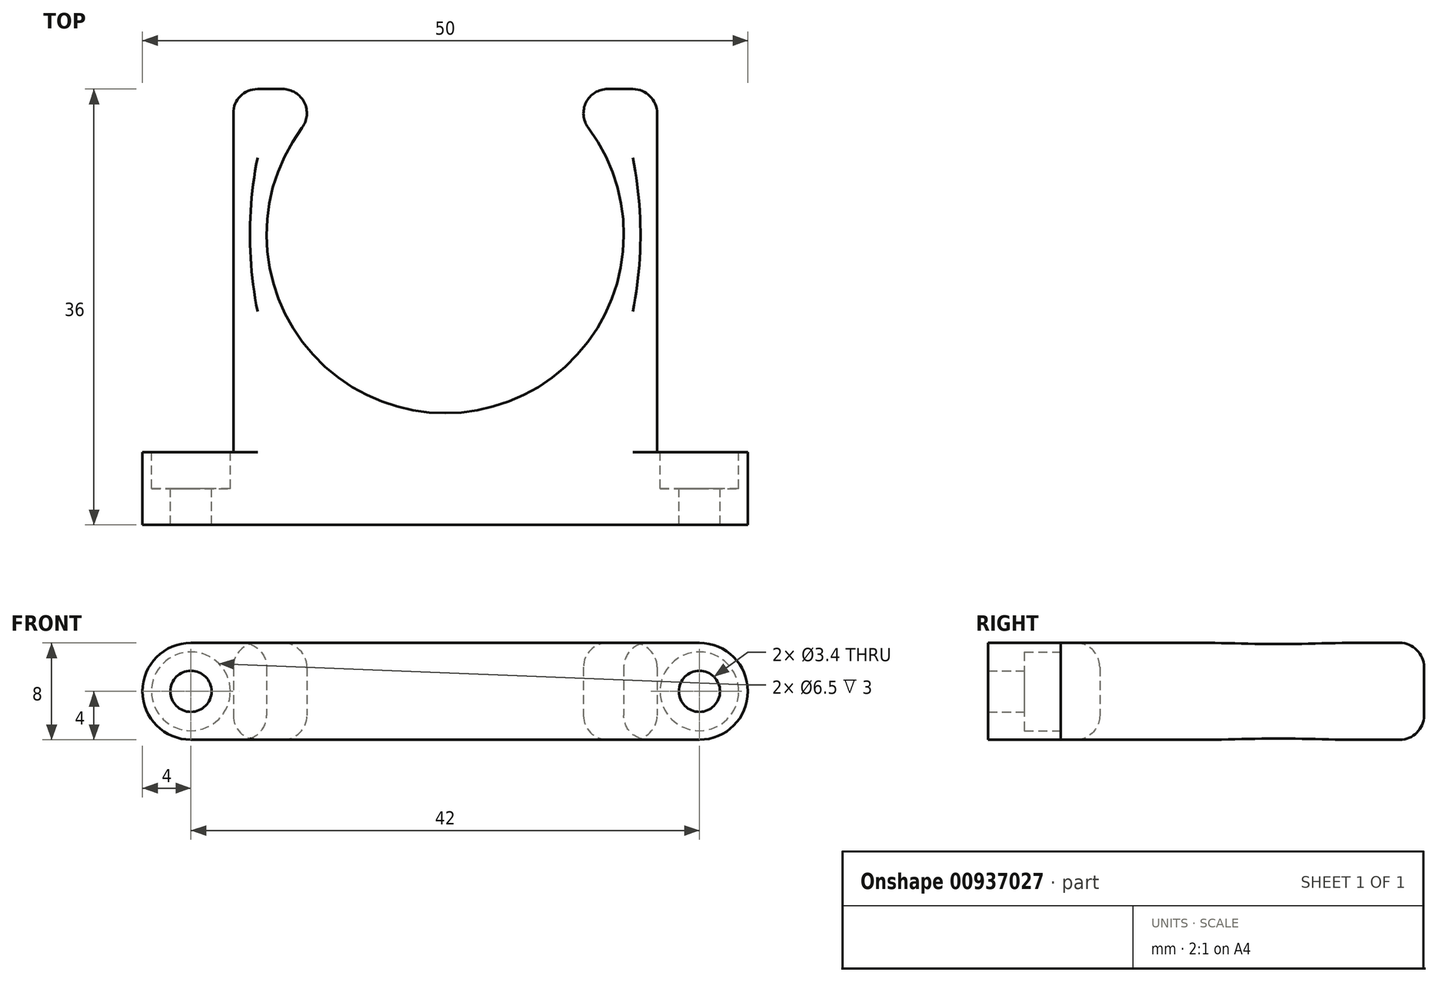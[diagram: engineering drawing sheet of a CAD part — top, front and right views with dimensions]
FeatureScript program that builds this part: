
annotation { "Feature Type Name" : "Feature", "Feature Type Description" : "" }
export const myFeature = defineFeature(function(context is Context, id is Id, definition is map)
    precondition{}
    {
        {
            var Q0;
            Q0=qCreatedBy(makeId("Top.planeOp"),FACE);
            var sketch = newSketch(context, id + "F0", { "sketchPlane" : qUnion([Q0])});
            skLineSegment(sketch, "E0", {"start": v(-25, 0) * mm, "end": v(25, 0) * mm});
            skLineSegment(sketch, "E1", {"start": v(-25, 0) * mm, "end": v(-25, 6) * mm});
            skLineSegment(sketch, "E2", {"start": v(-25, 6) * mm, "end": v(25, 6) * mm});
            skLineSegment(sketch, "E3", {"start": v(25, 6) * mm, "end": v(25, 0) * mm});
            skLineSegment(sketch, "E4.bottom", {"start": v(-17.5, 6) * mm, "end": v(17.5, 6) * mm});
            skLineSegment(sketch, "E4.top", {"start": v(-15.5, 36) * mm, "end": v(-13.42, 36) * mm});
            skLineSegment(sketch, "E4.left", {"start": v(-17.5, 6) * mm, "end": v(-17.5, 34) * mm});
            skLineSegment(sketch, "E4.right", {"start": v(17.5, 6) * mm, "end": v(17.5, 34) * mm});
            skArc(sketch, "E5", {"start": v(-11.82, 32.8) * mm, "mid": v(0, 9.23) * mm, "end": v(11.82, 32.8) * mm});
            skLineSegment(sketch, "E6", {"start": v(13.42, 36) * mm, "end": v(15.5, 36) * mm});
            skArc(sketch, "E7.filletArc", {"start": v(-11.82, 32.8) * mm, "mid": v(-11.63, 34.9) * mm, "end": v(-13.42, 36) * mm});
            skArc(sketch, "E8.filletArc", {"start": v(13.42, 36) * mm, "mid": v(11.63, 34.9) * mm, "end": v(11.82, 32.8) * mm});
            skPoint(sketch, "E9.visualSharp", {"position": v(17.5, 36) * mm});
            skArc(sketch, "E9.filletArc", {"start": v(17.5, 34) * mm, "mid": v(16.91, 35.41) * mm, "end": v(15.5, 36) * mm});
            skPoint(sketch, "E10.visualSharp", {"position": v(-17.5, 36) * mm});
            skArc(sketch, "E10.filletArc", {"start": v(-15.5, 36) * mm, "mid": v(-16.91, 35.41) * mm, "end": v(-17.5, 34) * mm});
            skSolve(sketch);
        }
        {
            var Q0;
            Q0 = qSketchRegion(id + "F0", true);
            extrude(context, id + "F1", {"entities" : qUnion([Q0]), "depth" : 8 * mm, "offsetDistance" : 25 * mm});
        }
        {
            var Q0;
            {var subQ0=sQuery(id+"F0.wireOp",EDGE,"E2");Q0=makeQuery(id+"F1.opExtrude","SWEPT_FACE",FACE,{"disambiguationData":[OSD([subQ0]),TDD([makeQuery(id+"F0.imprint","IMPRINT",EDGE,{"disambiguationData":[TD([[makeQuery(id+"F0.imprint","INTERSECT",VERTEX,{"derivedFrom":[subQ0,sQuery(id+"F0.wireOp",EDGE,"E3")]}),1.0]])],"derivedFrom":subQ0})])]});}
            var sketch = newSketch(context, id + "F2", { "sketchPlane" : qUnion([Q0])});
            skPoint(sketch, "E11", {"position": v(-21, 4) * mm});
            skSolve(sketch);
        }
        {
            var Q0;
            {var subQ0=sQuery(id+"F0.wireOp",EDGE,"E2");Q0=makeQuery(id+"F1.opExtrude","SWEPT_FACE",FACE,{"disambiguationData":[OSD([subQ0]),TDD([makeQuery(id+"F0.imprint","IMPRINT",EDGE,{"disambiguationData":[TD([[makeQuery(id+"F0.imprint","INTERSECT",VERTEX,{"derivedFrom":[sQuery(id+"F0.wireOp",EDGE,"E1"),subQ0]}),-1.0]])],"derivedFrom":subQ0})])]});}
            var sketch = newSketch(context, id + "F3", { "sketchPlane" : qUnion([Q0])});
            skPoint(sketch, "E12", {"position": v(21, 4) * mm});
            skPoint(sketch, "E12.positionSnap0", {"position": v(17.5, 4) * mm});
            skSolve(sketch);
        }
        {
            var Q0;
            Q0=sQuery(id+"F2.wireOp",VERTEX,"E11");
            var Q1;
            Q1=sQuery(id+"F3.wireOp",VERTEX,"E12");
            var Q2;
            Q2=makeQuery(id+"F1.opExtrude","SWEPT_BODY",BODY,{"disambiguationData":[OSD([sQuery(id+"F0.wireOp",EDGE,"E0"),sQuery(id+"F0.wireOp",EDGE,"E1"),sQuery(id+"F0.wireOp",EDGE,"E2"),sQuery(id+"F0.wireOp",EDGE,"E3"),sQuery(id+"F0.wireOp",EDGE,"E4.top"),sQuery(id+"F0.wireOp",EDGE,"E4.left"),sQuery(id+"F0.wireOp",EDGE,"E4.right"),sQuery(id+"F0.wireOp",EDGE,"E5"),sQuery(id+"F0.wireOp",EDGE,"E6"),sQuery(id+"F0.wireOp",EDGE,"E7.filletArc"),sQuery(id+"F0.wireOp",EDGE,"E8.filletArc"),sQuery(id+"F0.wireOp",EDGE,"E9.filletArc"),sQuery(id+"F0.wireOp",EDGE,"E10.filletArc")])]});
            hole(context, id + "F4", {"style" : HoleStyle.C_BORE, "endStyle" : HoleEndStyle.THROUGH, "standardTappedOrClearance" : lookupTablePath({ "fit" : "Normal", "standard" : "ISO", "size" : "M3", "type" : "Clearance" }), "standardBlindInLast" : lookupTablePath({ "fit" : "Normal", "standard" : "ISO", "engagement" : "75%", "pitch" : "0.5 mm", "size" : "M3", "type" : "Clearance & tapped" }), "holeDiameter" : 3.4 * mm, "cBoreDiameter" : 6.5 * mm, "cBoreDepth" : 3 * mm, "majorDiameter" : 5 * mm, "isTappedThrough" : true, "tappedDepth" : 12 * mm, "tapClearance" : 3, "startFromSketch" : true, "locations" : qUnion([Q0, Q1]), "scope" : qUnion([Q2])});
        }
        {
            var Q0;
            Q0=makeQuery(id+"F1.opExtrude","CAP_EDGE",EDGE,{"disambiguationData":[OSD([sQuery(id+"F0.wireOp",EDGE,"E5")])],"isStart":true});
            var Q1;
            Q1=makeQuery(id+"F1.opExtrude","CAP_EDGE",EDGE,{"disambiguationData":[OSD([sQuery(id+"F0.wireOp",EDGE,"E5")])],"isStart":false});
            fillet(context, id + "F5", {"entities" : qUnion([Q0, Q1]), "radius" : 2 * mm, "tangentPropagation" : true, "allowEdgeOverflow" : false});
        }
        {
            var Q0;
            Q0=makeQuery(id+"F1.opExtrude","CAP_EDGE",EDGE,{"disambiguationData":[OSD([sQuery(id+"F0.wireOp",EDGE,"E1")])],"isStart":true});
            var Q1;
            Q1=makeQuery(id+"F1.opExtrude","CAP_EDGE",EDGE,{"disambiguationData":[OSD([sQuery(id+"F0.wireOp",EDGE,"E1")])],"isStart":false});
            var Q2;
            Q2=makeQuery(id+"F1.opExtrude","CAP_EDGE",EDGE,{"disambiguationData":[OSD([sQuery(id+"F0.wireOp",EDGE,"E3")])],"isStart":true});
            var Q3;
            Q3=makeQuery(id+"F1.opExtrude","CAP_EDGE",EDGE,{"disambiguationData":[OSD([sQuery(id+"F0.wireOp",EDGE,"E3")])],"isStart":false});
            fillet(context, id + "F6", {"entities" : qUnion([Q0, Q1, Q2, Q3]), "radius" : 4 * mm, "tangentPropagation" : true, "allowEdgeOverflow" : false});
        }
    });
